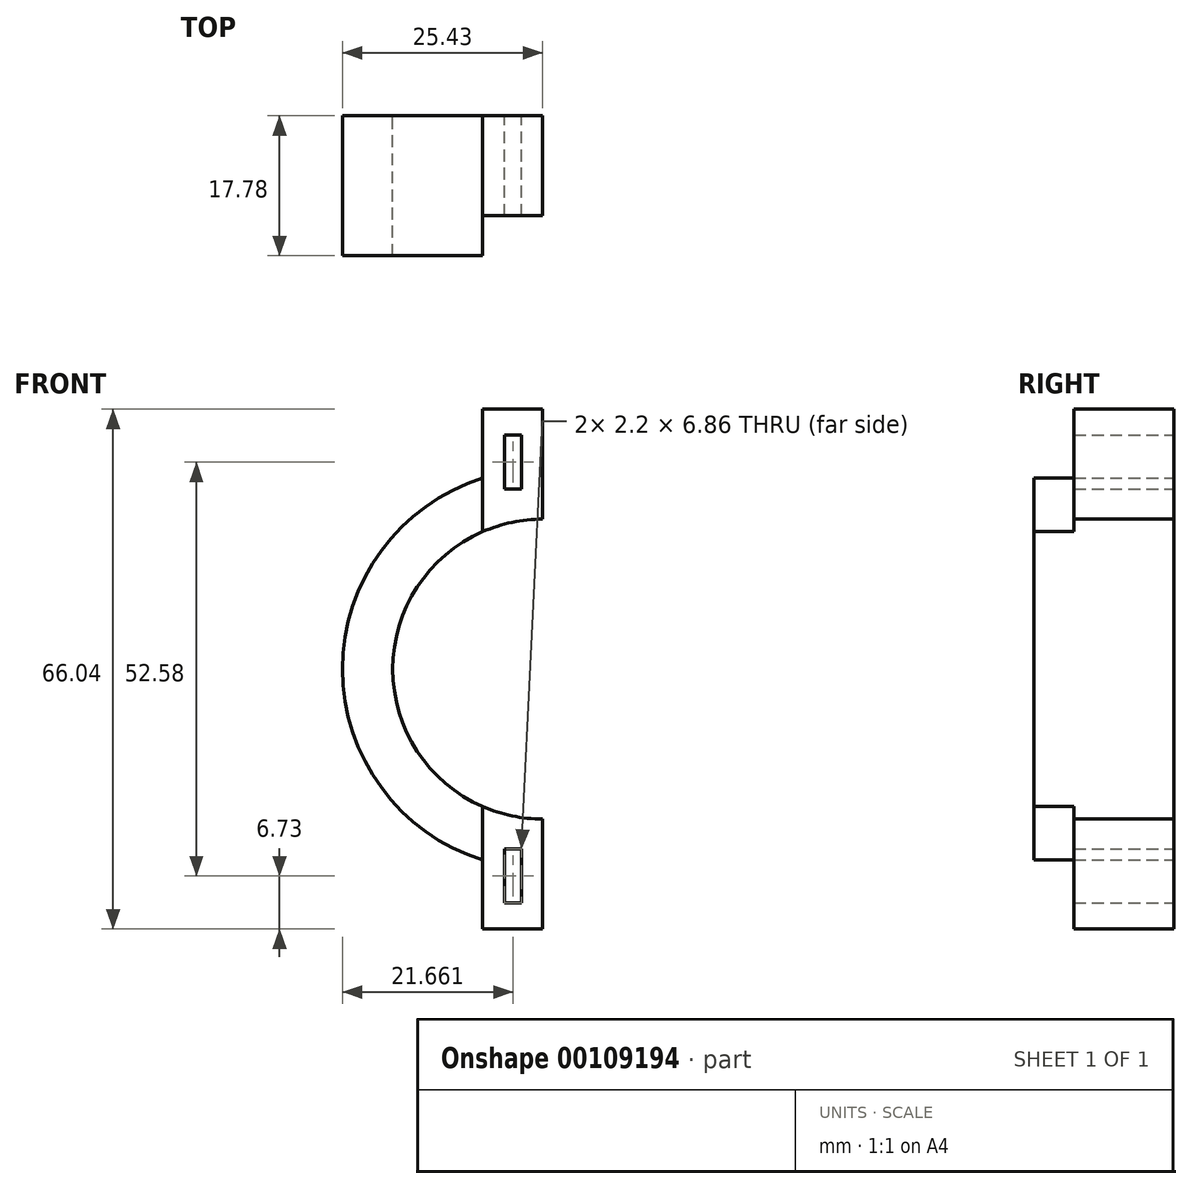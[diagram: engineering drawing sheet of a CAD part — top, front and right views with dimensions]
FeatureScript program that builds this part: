
annotation { "Feature Type Name" : "Feature", "Feature Type Description" : "" }
export const myFeature = defineFeature(function(context is Context, id is Id, definition is map)
    precondition{}
    {
        {
            var Q0;
            Q0=qCreatedBy(makeId("Front.planeOp"),FACE);
            var sketch = newSketch(context, id + "F0", { "sketchPlane" : qUnion([Q0])});
            skLineSegment(sketch, "E0", {"start": v(0, 42.41) * mm, "end": v(0, -42.81) * mm, "construction": true});
            skArc(sketch, "E1", {"start": v(0, 19.05) * mm, "mid": v(-19.05, 0) * mm, "end": v(0, -19.05) * mm});
            skArc(sketch, "E2", {"start": v(0, 25.43) * mm, "mid": v(-25.43, 0) * mm, "end": v(0, -25.43) * mm});
            skLineSegment(sketch, "E3.top", {"start": v(0, 33.02) * mm, "end": v(-7.62, 33.02) * mm});
            skLineSegment(sketch, "E3.left", {"start": v(0, 19.05) * mm, "end": v(0, 33.02) * mm});
            skLineSegment(sketch, "E3.right", {"start": v(-7.62, 17.46) * mm, "end": v(-7.62, 33.02) * mm});
            skLineSegment(sketch, "E4.MirrorCS", {"start": v(0, -33.02) * mm, "end": v(-7.62, -33.02) * mm});
            skLineSegment(sketch, "E5.MirrorCS", {"start": v(-7.62, -17.46) * mm, "end": v(-7.62, -33.02) * mm});
            skLineSegment(sketch, "E6.MirrorCS", {"start": v(0, -19.05) * mm, "end": v(0, -33.02) * mm});
            skLineSegment(sketch, "E7.bottom", {"start": v(-4.87, 29.72) * mm, "end": v(-2.67, 29.72) * mm});
            skLineSegment(sketch, "E7.top", {"start": v(-4.87, 22.86) * mm, "end": v(-2.67, 22.86) * mm});
            skLineSegment(sketch, "E7.left", {"start": v(-4.87, 29.72) * mm, "end": v(-4.87, 22.86) * mm});
            skLineSegment(sketch, "E7.right", {"start": v(-2.67, 29.72) * mm, "end": v(-2.67, 22.86) * mm});
            skLineSegment(sketch, "E8.MirrorCS", {"start": v(-4.87, -29.72) * mm, "end": v(-2.67, -29.72) * mm});
            skLineSegment(sketch, "E9.MirrorCS", {"start": v(-4.87, -29.72) * mm, "end": v(-4.87, -22.86) * mm});
            skLineSegment(sketch, "E10.MirrorCS", {"start": v(-2.67, -29.72) * mm, "end": v(-2.67, -22.86) * mm});
            skLineSegment(sketch, "E11.MirrorCS", {"start": v(-4.87, -22.86) * mm, "end": v(-2.67, -22.86) * mm});
            skPoint(sketch, "E12.middle.positionSnap0", {"position": v(-25.43, 0) * mm});
            skPoint(sketch, "E12.centerSnap0", {"position": v(-25.43, 0) * mm});
            skPoint(sketch, "E13", {"position": v(-19.05, 0) * mm});
            skSolve(sketch);
        }
        {
            var Q0;
            Q0=qSketchRegion(id+"F0",true);
            var Q1;
            {var subQ0=sQuery(id+"F0.wireOp",EDGE,"E3.right");var subQ1=sQuery(id+"F0.wireOp",EDGE,"E1");var subQ2=makeQuery(id+"F0.imprint","INTERSECT",VERTEX,{"derivedFrom":[subQ1,subQ0]});Q1=makeQuery(id+"F0.imprint","IMPRINT",FACE,{"disambiguationData":[TD([[makeQuery(id+"F0.imprint","IMPRINT",EDGE,{"disambiguationData":[TD([[subQ2,-1.0]])],"derivedFrom":subQ1}),-1.0]])]});}
            extrude(context, id + "F1", {"entities" : qUnion([Q0, Q1]), "depth" : 12.7 * mm});
        }
        {
            var Q0;
            {var subQ0=sQuery(id+"F0.wireOp",EDGE,"E3.right");var subQ1=sQuery(id+"F0.wireOp",EDGE,"E1");var subQ2=makeQuery(id+"F0.imprint","INTERSECT",VERTEX,{"derivedFrom":[subQ1,subQ0]});Q0=makeQuery(id+"F0.imprint","IMPRINT",FACE,{"disambiguationData":[TD([[makeQuery(id+"F0.imprint","IMPRINT",EDGE,{"disambiguationData":[TD([[subQ2,-1.0]])],"derivedFrom":subQ1}),-1.0]])]});}
            extrude(context, id + "F2", {"entities" : qUnion([Q0]), "operationType" : NewBodyOperationType.ADD, "depth" : 17.78 * mm});
        }
    });
